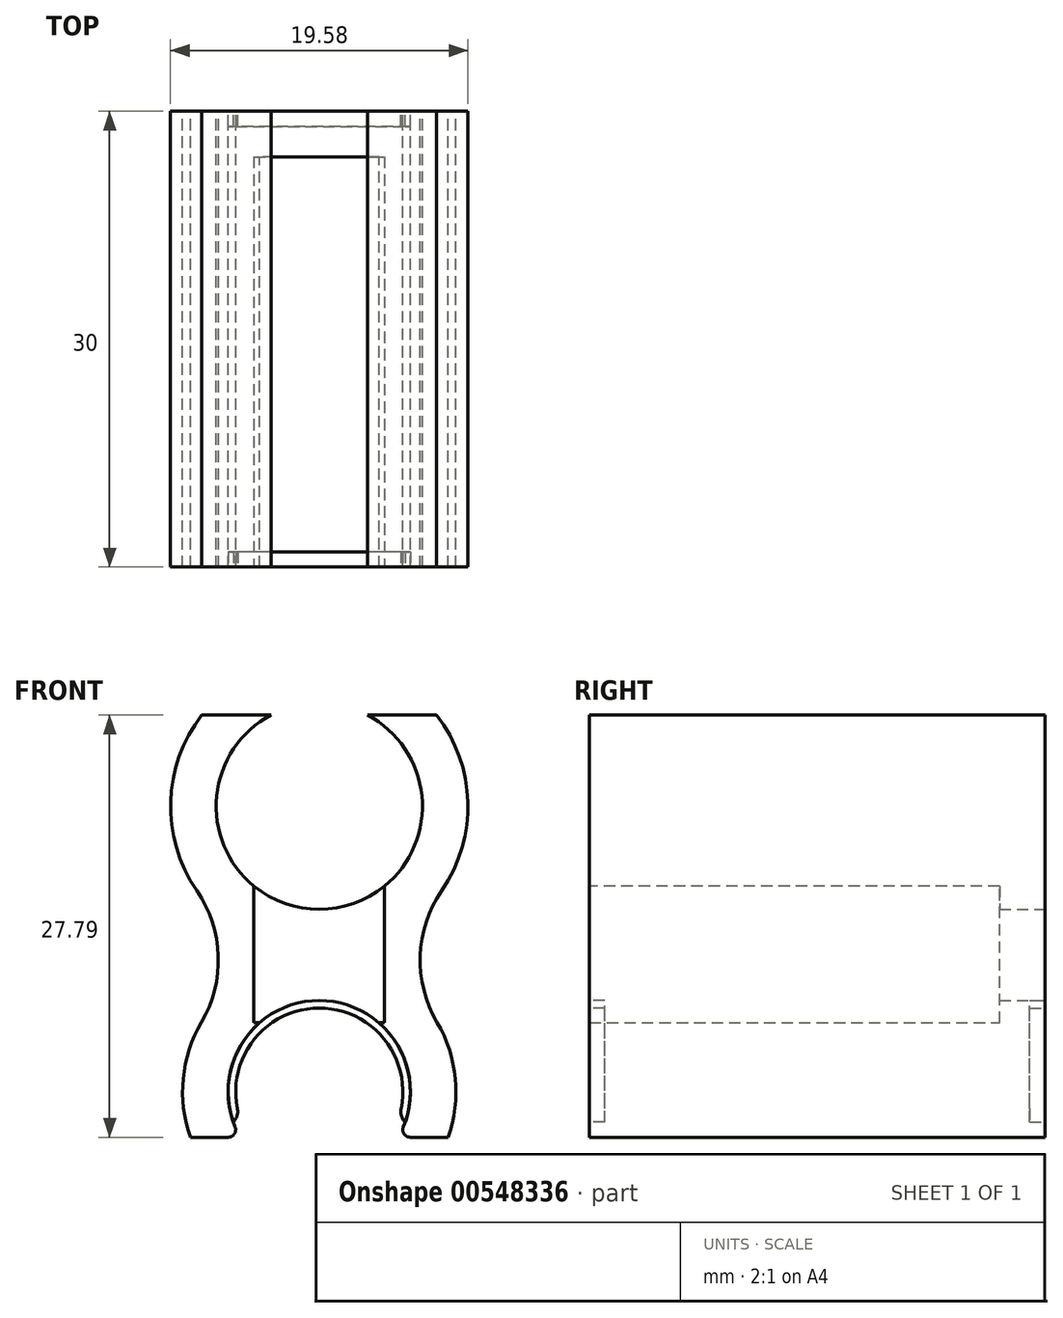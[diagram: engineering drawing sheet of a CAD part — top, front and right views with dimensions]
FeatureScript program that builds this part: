
annotation { "Feature Type Name" : "Feature", "Feature Type Description" : "" }
export const myFeature = defineFeature(function(context is Context, id is Id, definition is map)
    precondition{}
    {
        {
            var Q0;
            Q0=qCreatedBy(makeId("Front.planeOp"),FACE);
            var sketch = newSketch(context, id + "F0", { "sketchPlane" : qUnion([Q0])});
            skArc(sketch, "E0", {"start": v(-3.18, 15.79) * mm, "mid": v(0, 3) * mm, "end": v(3.18, 15.79) * mm});
            skArc(sketch, "E1", {"start": v(5.2, -12) * mm, "mid": v(0, -3) * mm, "end": v(-5.2, -12) * mm});
            skArc(sketch, "E2", {"start": v(-7.74, 15.79) * mm, "mid": v(-9.79, 10.07) * mm, "end": v(-8.07, 4.25) * mm});
            skArc(sketch, "E3", {"start": v(8.49, -12) * mm, "mid": v(8.96, -8.14) * mm, "end": v(7.76, -4.44) * mm});
            skArc(sketch, "E4", {"start": v(8.07, 4.25) * mm, "mid": v(6.65, -0.05) * mm, "end": v(7.76, -4.44) * mm});
            skArc(sketch, "E5", {"start": v(-7.76, -4.44) * mm, "mid": v(-6.65, -0.05) * mm, "end": v(-8.07, 4.25) * mm});
            skArc(sketch, "E6.trimOffspring", {"start": v(8.07, 4.25) * mm, "mid": v(9.79, 10.07) * mm, "end": v(7.74, 15.79) * mm});
            skArc(sketch, "E7.trimOffspring", {"start": v(-7.76, -4.44) * mm, "mid": v(-8.96, -8.14) * mm, "end": v(-8.49, -12) * mm});
            skLineSegment(sketch, "E8", {"start": v(-11.4, -9) * mm, "end": v(12.95, -9) * mm, "construction": true});
            skLineSegment(sketch, "E9", {"start": v(-8.49, -12) * mm, "end": v(-5.2, -12) * mm});
            skLineSegment(sketch, "E10", {"start": v(5.2, -12) * mm, "end": v(8.49, -12) * mm});
            skLineSegment(sketch, "E11", {"start": v(-7.74, 15.79) * mm, "end": v(-3.18, 15.79) * mm});
            skLineSegment(sketch, "E12", {"start": v(3.18, 15.79) * mm, "end": v(7.74, 15.79) * mm});
            skLineSegment(sketch, "E13", {"start": v(-11.57, 9.79) * mm, "end": v(11.68, 9.79) * mm, "construction": true});
            skSolve(sketch);
        }
        {
            var Q0;
            Q0 = qSketchRegion(id + "F0", true);
            extrude(context, id + "F1", {"entities" : qUnion([Q0]), "depth" : 30 * mm, "offsetDistance" : 25.4 * mm});
        }
        {
            var Q0;
            Q0=makeQuery(id+"F1.opExtrude","CAP_FACE",FACE,{"disambiguationData":[OSD([sQuery(id+"F0.wireOp",EDGE,"E0"),sQuery(id+"F0.wireOp",EDGE,"E1"),sQuery(id+"F0.wireOp",EDGE,"E2"),sQuery(id+"F0.wireOp",EDGE,"E3"),sQuery(id+"F0.wireOp",EDGE,"E4"),sQuery(id+"F0.wireOp",EDGE,"E5"),sQuery(id+"F0.wireOp",EDGE,"E6.trimOffspring"),sQuery(id+"F0.wireOp",EDGE,"E7.trimOffspring"),sQuery(id+"F0.wireOp",EDGE,"E9"),sQuery(id+"F0.wireOp",EDGE,"E10"),sQuery(id+"F0.wireOp",EDGE,"E11"),sQuery(id+"F0.wireOp",EDGE,"E12")])],"isStart":false});
            var sketch = newSketch(context, id + "F2", { "sketchPlane" : qUnion([Q0])});
            skLineSegment(sketch, "E14", {"start": v(-4.3, 4.54) * mm, "end": v(-4.3, -4.46) * mm});
            skLineSegment(sketch, "E15", {"start": v(-4.3, -4.46) * mm, "end": v(4.3, -4.46) * mm});
            skLineSegment(sketch, "E16", {"start": v(4.3, -4.46) * mm, "end": v(4.3, 4.54) * mm});
            skArc(sketch, "E17.0", {"start": v(-4.3, 4.54) * mm, "mid": v(0, 3) * mm, "end": v(4.3, 4.54) * mm});
            skPoint(sketch, "E18.orphan", {"position": v(-3.18, 15.79) * mm});
            skPoint(sketch, "E19.orphan", {"position": v(3.18, 15.79) * mm});
            skLineSegment(sketch, "E20", {"start": v(0, 7.63) * mm, "end": v(0, -8.43) * mm, "construction": true});
            skSolve(sketch);
        }
        {
            var Q0;
            Q0 = qSketchRegion(id + "F2", true);
            extrude(context, id + "F3", {"entities" : qUnion([Q0]), "operationType" : NewBodyOperationType.REMOVE, "oppositeDirection" : true, "depth" : 27 * mm, "offsetDistance" : 25.4 * mm});
        }
        {
            var Q0;
            Q0=makeQuery(id+"F1.opExtrude","CAP_FACE",FACE,{"disambiguationData":[OSD([sQuery(id+"F0.wireOp",EDGE,"E0"),sQuery(id+"F0.wireOp",EDGE,"E1"),sQuery(id+"F0.wireOp",EDGE,"E2"),sQuery(id+"F0.wireOp",EDGE,"E3"),sQuery(id+"F0.wireOp",EDGE,"E4"),sQuery(id+"F0.wireOp",EDGE,"E5"),sQuery(id+"F0.wireOp",EDGE,"E6.trimOffspring"),sQuery(id+"F0.wireOp",EDGE,"E7.trimOffspring"),sQuery(id+"F0.wireOp",EDGE,"E9"),sQuery(id+"F0.wireOp",EDGE,"E10"),sQuery(id+"F0.wireOp",EDGE,"E11"),sQuery(id+"F0.wireOp",EDGE,"E12")])],"isStart":false});
            var sketch = newSketch(context, id + "F4", { "sketchPlane" : qUnion([Q0])});
            skArc(sketch, "E21.0", {"start": v(5.66, -11) * mm, "mid": v(0, -3) * mm, "end": v(-5.66, -11) * mm});
            skArc(sketch, "E22.0", {"start": v(5.12, -11) * mm, "mid": v(0, -3.5) * mm, "end": v(-5.12, -11) * mm});
            skLineSegment(sketch, "E23", {"start": v(-5.12, -11) * mm, "end": v(-5.66, -11) * mm});
            skLineSegment(sketch, "E24", {"start": v(5.12, -11) * mm, "end": v(5.66, -11) * mm});
            skSolve(sketch);
        }
        {
            var Q0;
            Q0 = qSketchRegion(id + "F4", true);
            extrude(context, id + "F5", {"entities" : qUnion([Q0]), "oppositeDirection" : true, "depth" : 1 * mm, "offsetDistance" : 25.4 * mm});
        }
        {
            var Q0;
            Q0=makeQuery(id+"F1.opExtrude","CAP_FACE",FACE,{"disambiguationData":[OSD([sQuery(id+"F0.wireOp",EDGE,"E0"),sQuery(id+"F0.wireOp",EDGE,"E1"),sQuery(id+"F0.wireOp",EDGE,"E2"),sQuery(id+"F0.wireOp",EDGE,"E3"),sQuery(id+"F0.wireOp",EDGE,"E4"),sQuery(id+"F0.wireOp",EDGE,"E5"),sQuery(id+"F0.wireOp",EDGE,"E6.trimOffspring"),sQuery(id+"F0.wireOp",EDGE,"E7.trimOffspring"),sQuery(id+"F0.wireOp",EDGE,"E9"),sQuery(id+"F0.wireOp",EDGE,"E10"),sQuery(id+"F0.wireOp",EDGE,"E11"),sQuery(id+"F0.wireOp",EDGE,"E12")])],"isStart":true});
            var sketch = newSketch(context, id + "F6", { "sketchPlane" : qUnion([Q0])});
            skArc(sketch, "E25.0", {"start": v(-5.66, -11) * mm, "mid": v(0, -3) * mm, "end": v(5.66, -11) * mm});
            skArc(sketch, "E26.0", {"start": v(-5.12, -11) * mm, "mid": v(0, -3.5) * mm, "end": v(5.12, -11) * mm});
            skLineSegment(sketch, "E27", {"start": v(-5.66, -11) * mm, "end": v(-5.12, -11) * mm});
            skLineSegment(sketch, "E28", {"start": v(5.12, -11) * mm, "end": v(5.66, -11) * mm});
            skSolve(sketch);
        }
        {
            var Q0;
            Q0 = qSketchRegion(id + "F6", true);
            extrude(context, id + "F7", {"entities" : qUnion([Q0]), "oppositeDirection" : true, "depth" : 1 * mm, "offsetDistance" : 25.4 * mm});
        }
        {
            var Q0;
            Q0=makeQuery(id+"F7.opExtrude","SWEPT_EDGE",EDGE,{"disambiguationData":[OSD([sQuery(id+"F6.wireOp",EDGE,"E26.0"),sQuery(id+"F6.wireOp",EDGE,"E27")])]});
            var Q1;
            Q1=makeQuery(id+"F5.opExtrude","SWEPT_EDGE",EDGE,{"disambiguationData":[OSD([sQuery(id+"F4.wireOp",EDGE,"E22.0"),sQuery(id+"F4.wireOp",EDGE,"E24")])]});
            var Q2;
            Q2=makeQuery(id+"F7.opExtrude","SWEPT_EDGE",EDGE,{"disambiguationData":[OSD([sQuery(id+"F6.wireOp",EDGE,"E26.0"),sQuery(id+"F6.wireOp",EDGE,"E28")])]});
            var Q3;
            Q3=makeQuery(id+"F5.opExtrude","SWEPT_EDGE",EDGE,{"disambiguationData":[OSD([sQuery(id+"F4.wireOp",EDGE,"E22.0"),sQuery(id+"F4.wireOp",EDGE,"E23")])]});
            fillet(context, id + "F8", {"entities" : qUnion([Q0, Q1, Q2, Q3]), "radius" : 1 * mm, "tangentPropagation" : true, "allowEdgeOverflow" : false});
        }
        {
            var Q0;
            Q0=makeQuery(id+"F1.opExtrude","SWEPT_EDGE",EDGE,{"disambiguationData":[OSD([sQuery(id+"F0.wireOp",EDGE,"E1"),sQuery(id+"F0.wireOp",EDGE,"E10")])]});
            var Q1;
            Q1=makeQuery(id+"F1.opExtrude","SWEPT_EDGE",EDGE,{"disambiguationData":[OSD([sQuery(id+"F0.wireOp",EDGE,"E1"),sQuery(id+"F0.wireOp",EDGE,"E9")])]});
            fillet(context, id + "F9", {"entities" : qUnion([Q0, Q1]), "radius" : 0.5 * mm, "tangentPropagation" : true, "allowEdgeOverflow" : false});
        }
    });
